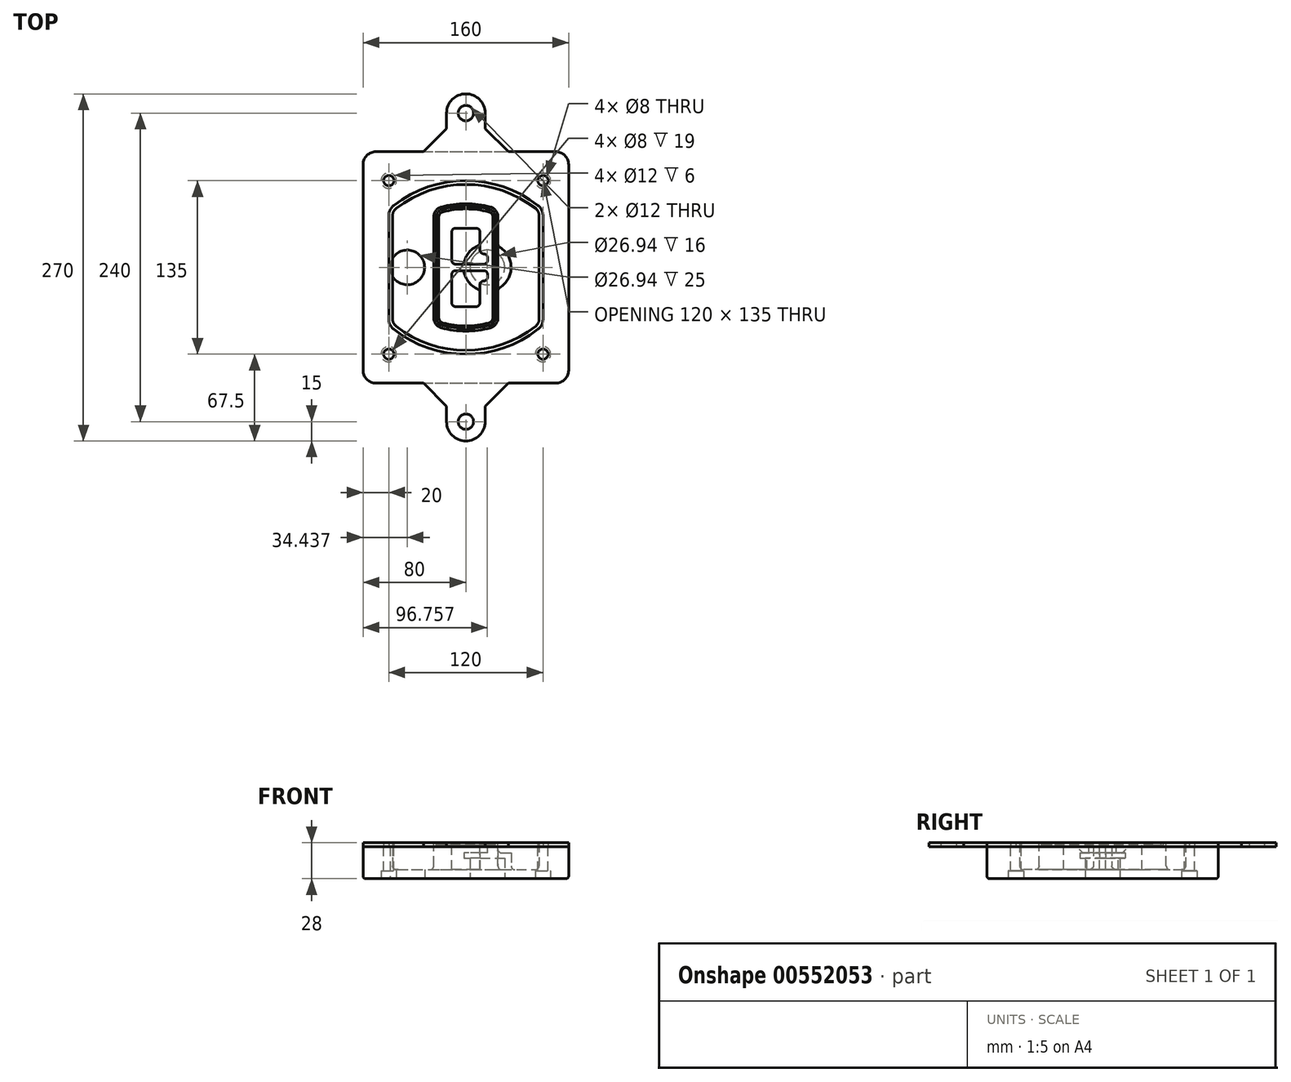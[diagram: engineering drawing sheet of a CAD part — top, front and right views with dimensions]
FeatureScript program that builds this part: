
annotation { "Feature Type Name" : "Feature", "Feature Type Description" : "" }
export const myFeature = defineFeature(function(context is Context, id is Id, definition is map)
    precondition{}
    {
        {
            var Q0;
            Q0=qCreatedBy(makeId("Top.planeOp"),FACE);
            var sketch = newSketch(context, id + "F0", { "sketchPlane" : qUnion([Q0])});
            skPoint(sketch, "E0.rect.middle", {"position": v(0, 0) * mm});
            skLineSegment(sketch, "E1.bottom", {"start": v(-70, -90) * mm, "end": v(70, -90) * mm});
            skLineSegment(sketch, "E1.top", {"start": v(-70, 90) * mm, "end": v(70, 90) * mm});
            skLineSegment(sketch, "E1.left", {"start": v(-80, -80) * mm, "end": v(-80, 80) * mm});
            skLineSegment(sketch, "E1.right", {"start": v(80, -80) * mm, "end": v(80, 80) * mm});
            skLineSegment(sketch, "E2", {"start": v(-80, 90) * mm, "end": v(80, -90) * mm, "construction": true});
            skLineSegment(sketch, "E3", {"start": v(80, 90) * mm, "end": v(-80, -90) * mm, "construction": true});
            skCircle(sketch, "E4", {"center": v(-60, 67.5) * mm, "radius": 4 * mm});
            skCircle(sketch, "E5", {"center": v(60, 67.5) * mm, "radius": 4 * mm});
            skCircle(sketch, "E6", {"center": v(60, -67.5) * mm, "radius": 4 * mm});
            skCircle(sketch, "E7", {"center": v(-60, -67.5) * mm, "radius": 4 * mm});
            skLineSegment(sketch, "E8", {"start": v(-60, 67.5) * mm, "end": v(60, 67.5) * mm, "construction": true});
            skLineSegment(sketch, "E9", {"start": v(60, 67.5) * mm, "end": v(60, -67.5) * mm, "construction": true});
            skLineSegment(sketch, "E10", {"start": v(60, -67.5) * mm, "end": v(-60, -67.5) * mm, "construction": true});
            skLineSegment(sketch, "E11", {"start": v(-60, -67.5) * mm, "end": v(-60, 67.5) * mm, "construction": true});
            skLineSegment(sketch, "E12", {"start": v(-60, 40.3) * mm, "end": v(-60, -40.3) * mm});
            skLineSegment(sketch, "E13", {"start": v(60, 40.3) * mm, "end": v(60, -40.3) * mm});
            skArc(sketch, "E14", {"start": v(56.15, 48.18) * mm, "mid": v(0, 67.5) * mm, "end": v(-56.15, 48.18) * mm});
            skArc(sketch, "E15", {"start": v(-56.15, -48.18) * mm, "mid": v(0, -67.5) * mm, "end": v(56.15, -48.18) * mm});
            skLineSegment(sketch, "E16", {"start": v(-60, 0) * mm, "end": v(60, 0) * mm, "construction": true});
            skPoint(sketch, "E17.visualSharp", {"position": v(-60, -45) * mm});
            skArc(sketch, "E17.filletArc", {"start": v(-60, -40.3) * mm, "mid": v(-58.99, -44.68) * mm, "end": v(-56.15, -48.18) * mm});
            skPoint(sketch, "E18.visualSharp", {"position": v(-60, 45) * mm});
            skArc(sketch, "E18.filletArc", {"start": v(-56.15, 48.18) * mm, "mid": v(-58.99, 44.68) * mm, "end": v(-60, 40.3) * mm});
            skPoint(sketch, "E19.visualSharp", {"position": v(60, 45) * mm});
            skArc(sketch, "E19.filletArc", {"start": v(60, 40.3) * mm, "mid": v(58.99, 44.68) * mm, "end": v(56.15, 48.18) * mm});
            skPoint(sketch, "E20.visualSharp", {"position": v(60, -45) * mm});
            skArc(sketch, "E20.filletArc", {"start": v(56.15, -48.18) * mm, "mid": v(58.99, -44.68) * mm, "end": v(60, -40.3) * mm});
            skPoint(sketch, "E21.visualSharp", {"position": v(-80, 90) * mm});
            skArc(sketch, "E21.filletArc", {"start": v(-70, 90) * mm, "mid": v(-77.07, 87.07) * mm, "end": v(-80, 80) * mm});
            skPoint(sketch, "E22.visualSharp", {"position": v(80, 90) * mm});
            skArc(sketch, "E22.filletArc", {"start": v(80, 80) * mm, "mid": v(77.07, 87.07) * mm, "end": v(70, 90) * mm});
            skPoint(sketch, "E23.visualSharp", {"position": v(80, -90) * mm});
            skArc(sketch, "E23.filletArc", {"start": v(70, -90) * mm, "mid": v(77.07, -87.07) * mm, "end": v(80, -80) * mm});
            skPoint(sketch, "E24.visualSharp", {"position": v(-80, -90) * mm});
            skArc(sketch, "E24.filletArc", {"start": v(-80, -80) * mm, "mid": v(-77.07, -87.07) * mm, "end": v(-70, -90) * mm});
            skArc(sketch, "E25.0", {"start": v(57, 40.3) * mm, "mid": v(56.3, 43.36) * mm, "end": v(54.3, 45.81) * mm});
            skLineSegment(sketch, "E25.1", {"start": v(57, 40.3) * mm, "end": v(57, -40.3) * mm});
            skArc(sketch, "E25.2", {"start": v(54.3, -45.81) * mm, "mid": v(56.3, -43.36) * mm, "end": v(57, -40.3) * mm});
            skArc(sketch, "E25.3", {"start": v(-54.3, -45.81) * mm, "mid": v(0, -64.5) * mm, "end": v(54.3, -45.81) * mm});
            skArc(sketch, "E25.4", {"start": v(-57, -40.3) * mm, "mid": v(-56.3, -43.36) * mm, "end": v(-54.3, -45.81) * mm});
            skArc(sketch, "E25.5", {"start": v(54.3, 45.81) * mm, "mid": v(0, 64.5) * mm, "end": v(-54.3, 45.81) * mm});
            skLineSegment(sketch, "E25.6", {"start": v(-57, 40.3) * mm, "end": v(-57, -40.3) * mm});
            skArc(sketch, "E25.7", {"start": v(-54.3, 45.81) * mm, "mid": v(-56.3, 43.36) * mm, "end": v(-57, 40.3) * mm});
            skArc(sketch, "E26.0", {"start": v(-58.62, 51.33) * mm, "mid": v(-62.58, 46.43) * mm, "end": v(-64, 40.3) * mm});
            skArc(sketch, "E26.1", {"start": v(58.62, 51.33) * mm, "mid": v(0, 71.5) * mm, "end": v(-58.62, 51.33) * mm});
            skArc(sketch, "E26.2", {"start": v(64, 40.3) * mm, "mid": v(62.58, 46.43) * mm, "end": v(58.62, 51.33) * mm});
            skLineSegment(sketch, "E26.3", {"start": v(64, 40.3) * mm, "end": v(64, -40.3) * mm});
            skArc(sketch, "E26.4", {"start": v(58.62, -51.33) * mm, "mid": v(62.58, -46.43) * mm, "end": v(64, -40.3) * mm});
            skLineSegment(sketch, "E26.5", {"start": v(-64, 40.3) * mm, "end": v(-64, -40.3) * mm});
            skArc(sketch, "E26.6", {"start": v(-58.62, -51.33) * mm, "mid": v(0, -71.5) * mm, "end": v(58.62, -51.33) * mm});
            skArc(sketch, "E26.7", {"start": v(-64, -40.3) * mm, "mid": v(-62.58, -46.43) * mm, "end": v(-58.62, -51.33) * mm});
            skSolve(sketch);
        }
        {
            var Q0;
            Q0=makeQuery(id+"F0.imprint","IMPRINT",FACE,{"disambiguationData":[TD([[makeQuery(id+"F0.imprint","IMPRINT",EDGE,{"derivedFrom":sQuery(id+"F0.wireOp",EDGE,"E1.bottom")}),1.0]])]});
            var Q1;
            Q1=makeQuery(id+"F0.imprint","IMPRINT",FACE,{"disambiguationData":[TD([[makeQuery(id+"F0.imprint","IMPRINT",EDGE,{"derivedFrom":sQuery(id+"F0.wireOp",EDGE,"E12")}),1.0]])]});
            var Q2;
            Q2=makeQuery(id+"F0.imprint","IMPRINT",FACE,{"disambiguationData":[TD([[makeQuery(id+"F0.imprint","IMPRINT",EDGE,{"derivedFrom":sQuery(id+"F0.wireOp",EDGE,"E25.0")}),1.0]])]});
            var Q3;
            Q3=makeQuery(id+"F0.imprint","IMPRINT",FACE,{"disambiguationData":[TD([[makeQuery(id+"F0.imprint","IMPRINT",EDGE,{"derivedFrom":sQuery(id+"F0.wireOp",EDGE,"E12")}),-1.0]])]});
            extrude(context, id + "F1", {"entities" : qUnion([Q0, Q1, Q2, Q3]), "oppositeDirection" : true, "depth" : 25 * mm});
        }
        {
            var Q0;
            Q0=makeQuery(id+"F0.imprint","IMPRINT",FACE,{"disambiguationData":[TD([[makeQuery(id+"F0.imprint","IMPRINT",EDGE,{"derivedFrom":sQuery(id+"F0.wireOp",EDGE,"E12")}),1.0]])]});
            extrude(context, id + "F2", {"entities" : qUnion([Q0]), "operationType" : NewBodyOperationType.ADD, "depth" : 3 * mm});
        }
        {
            var Q0;
            Q0=makeQuery(id+"F0.imprint","IMPRINT",FACE,{"disambiguationData":[TD([[makeQuery(id+"F0.imprint","IMPRINT",EDGE,{"derivedFrom":sQuery(id+"F0.wireOp",EDGE,"E25.0")}),1.0]])]});
            extrude(context, id + "F3", {"entities" : qUnion([Q0]), "operationType" : NewBodyOperationType.REMOVE, "oppositeDirection" : true, "depth" : 18 * mm});
        }
        {
            var Q0;
            Q0=makeQuery(id+"F2.opExtrude","CAP_FACE",FACE,{"disambiguationData":[OSD([sQuery(id+"F0.wireOp",EDGE,"E12"),sQuery(id+"F0.wireOp",EDGE,"E13"),sQuery(id+"F0.wireOp",EDGE,"E14"),sQuery(id+"F0.wireOp",EDGE,"E15"),sQuery(id+"F0.wireOp",EDGE,"E17.filletArc"),sQuery(id+"F0.wireOp",EDGE,"E18.filletArc"),sQuery(id+"F0.wireOp",EDGE,"E19.filletArc"),sQuery(id+"F0.wireOp",EDGE,"E20.filletArc"),sQuery(id+"F0.wireOp",EDGE,"E25.0"),sQuery(id+"F0.wireOp",EDGE,"E25.1"),sQuery(id+"F0.wireOp",EDGE,"E25.2"),sQuery(id+"F0.wireOp",EDGE,"E25.3"),sQuery(id+"F0.wireOp",EDGE,"E25.4"),sQuery(id+"F0.wireOp",EDGE,"E25.5"),sQuery(id+"F0.wireOp",EDGE,"E25.6"),sQuery(id+"F0.wireOp",EDGE,"E25.7")])],"isStart":false});
            var sketch = newSketch(context, id + "F4", { "sketchPlane" : qUnion([Q0])});
            skArc(sketch, "E27.0", {"start": v(-19.08, -46.97) * mm, "mid": v(0, -49.5) * mm, "end": v(19.08, -46.97) * mm});
            skArc(sketch, "E28.0", {"start": v(19.08, 46.97) * mm, "mid": v(0, 49.5) * mm, "end": v(-19.08, 46.97) * mm});
            skLineSegment(sketch, "E29", {"start": v(-25, 39.25) * mm, "end": v(-25, -39.25) * mm});
            skLineSegment(sketch, "E30", {"start": v(25, 39.25) * mm, "end": v(25, -39.25) * mm});
            skLineSegment(sketch, "E31", {"start": v(-25, 45.1) * mm, "end": v(25, 45.1) * mm, "construction": true});
            skLineSegment(sketch, "E32", {"start": v(-25, -45.1) * mm, "end": v(25, -45.1) * mm, "construction": true});
            skPoint(sketch, "E33.visualSharp", {"position": v(-25, 45.1) * mm});
            skArc(sketch, "E33.filletArc", {"start": v(-19.08, 46.97) * mm, "mid": v(-23.35, 44.11) * mm, "end": v(-25, 39.25) * mm});
            skPoint(sketch, "E34.visualSharp", {"position": v(25, 45.1) * mm});
            skArc(sketch, "E34.filletArc", {"start": v(25, 39.25) * mm, "mid": v(23.35, 44.11) * mm, "end": v(19.08, 46.97) * mm});
            skPoint(sketch, "E35.visualSharp", {"position": v(25, -45.1) * mm});
            skArc(sketch, "E35.filletArc", {"start": v(19.08, -46.97) * mm, "mid": v(23.35, -44.11) * mm, "end": v(25, -39.25) * mm});
            skPoint(sketch, "E36.visualSharp", {"position": v(-25, -45.1) * mm});
            skArc(sketch, "E36.filletArc", {"start": v(-25, -39.25) * mm, "mid": v(-23.35, -44.11) * mm, "end": v(-19.08, -46.97) * mm});
            skArc(sketch, "E37.0", {"start": v(54.3, 45.81) * mm, "mid": v(0, 64.5) * mm, "end": v(-54.3, 45.81) * mm});
            skArc(sketch, "E37.1", {"start": v(-54.3, 45.81) * mm, "mid": v(-56.3, 43.36) * mm, "end": v(-57, 40.3) * mm});
            skLineSegment(sketch, "E37.2", {"start": v(-57, 40.3) * mm, "end": v(-57, -40.3) * mm});
            skArc(sketch, "E37.3", {"start": v(-57, -40.3) * mm, "mid": v(-56.3, -43.36) * mm, "end": v(-54.3, -45.81) * mm});
            skArc(sketch, "E37.4", {"start": v(-54.3, -45.81) * mm, "mid": v(0, -64.5) * mm, "end": v(54.3, -45.81) * mm});
            skArc(sketch, "E37.5", {"start": v(54.3, -45.81) * mm, "mid": v(56.3, -43.36) * mm, "end": v(57, -40.3) * mm});
            skLineSegment(sketch, "E37.6", {"start": v(57, 40.3) * mm, "end": v(57, -40.3) * mm});
            skArc(sketch, "E37.7", {"start": v(57, 40.3) * mm, "mid": v(56.3, 43.36) * mm, "end": v(54.3, 45.81) * mm});
            skLineSegment(sketch, "E38.0", {"start": v(23, 39.25) * mm, "end": v(23, -39.25) * mm});
            skArc(sketch, "E38.1", {"start": v(18.56, -45.04) * mm, "mid": v(21.76, -42.9) * mm, "end": v(23, -39.25) * mm});
            skArc(sketch, "E38.2", {"start": v(-18.56, -45.04) * mm, "mid": v(0, -47.5) * mm, "end": v(18.56, -45.04) * mm});
            skArc(sketch, "E38.3", {"start": v(-23, -39.25) * mm, "mid": v(-21.76, -42.9) * mm, "end": v(-18.56, -45.04) * mm});
            skLineSegment(sketch, "E38.4", {"start": v(-23, 39.25) * mm, "end": v(-23, -39.25) * mm});
            skArc(sketch, "E38.5", {"start": v(23, 39.25) * mm, "mid": v(21.76, 42.9) * mm, "end": v(18.56, 45.04) * mm});
            skArc(sketch, "E38.6", {"start": v(-18.56, 45.04) * mm, "mid": v(-21.76, 42.9) * mm, "end": v(-23, 39.25) * mm});
            skArc(sketch, "E38.7", {"start": v(18.56, 45.04) * mm, "mid": v(0, 47.5) * mm, "end": v(-18.56, 45.04) * mm});
            skArc(sketch, "E39.0", {"start": v(21, 39.25) * mm, "mid": v(20.18, 41.68) * mm, "end": v(18.04, 43.1) * mm});
            skLineSegment(sketch, "E39.1", {"start": v(21, 39.25) * mm, "end": v(21, -39.25) * mm});
            skArc(sketch, "E39.2", {"start": v(18.04, -43.1) * mm, "mid": v(20.18, -41.68) * mm, "end": v(21, -39.25) * mm});
            skArc(sketch, "E39.3", {"start": v(-18.04, -43.1) * mm, "mid": v(0, -45.5) * mm, "end": v(18.04, -43.1) * mm});
            skArc(sketch, "E39.4", {"start": v(-21, -39.25) * mm, "mid": v(-20.18, -41.68) * mm, "end": v(-18.04, -43.1) * mm});
            skArc(sketch, "E39.5", {"start": v(18.04, 43.1) * mm, "mid": v(0, 45.5) * mm, "end": v(-18.04, 43.1) * mm});
            skLineSegment(sketch, "E39.6", {"start": v(-21, 39.25) * mm, "end": v(-21, -39.25) * mm});
            skArc(sketch, "E39.7", {"start": v(-18.04, 43.1) * mm, "mid": v(-20.18, 41.68) * mm, "end": v(-21, 39.25) * mm});
            skLineSegment(sketch, "E40", {"start": v(-25, 0) * mm, "end": v(25, 0) * mm, "construction": true});
            skLineSegment(sketch, "E41", {"start": v(-11, 5.5) * mm, "end": v(-11, 27.5) * mm});
            skLineSegment(sketch, "E42", {"start": v(-8, 30.5) * mm, "end": v(8, 30.5) * mm});
            skLineSegment(sketch, "E43", {"start": v(11, 27.5) * mm, "end": v(11, 13.5) * mm});
            skLineSegment(sketch, "E44", {"start": v(14, 10.5) * mm, "end": v(14, 10.5) * mm});
            skLineSegment(sketch, "E45", {"start": v(17, 7.5) * mm, "end": v(17, 5.5) * mm});
            skLineSegment(sketch, "E46", {"start": v(14, 2.5) * mm, "end": v(-8, 2.5) * mm});
            skPoint(sketch, "E47.visualSharp", {"position": v(-11, 30.5) * mm});
            skArc(sketch, "E47.filletArc", {"start": v(-8, 30.5) * mm, "mid": v(-10.12, 29.62) * mm, "end": v(-11, 27.5) * mm});
            skPoint(sketch, "E48.visualSharp", {"position": v(11, 30.5) * mm});
            skArc(sketch, "E48.filletArc", {"start": v(11, 27.5) * mm, "mid": v(10.12, 29.62) * mm, "end": v(8, 30.5) * mm});
            skPoint(sketch, "E49.visualSharp", {"position": v(11, 10.5) * mm});
            skArc(sketch, "E49.filletArc", {"start": v(11, 13.5) * mm, "mid": v(11.88, 11.38) * mm, "end": v(14, 10.5) * mm});
            skPoint(sketch, "E50.visualSharp", {"position": v(17, 10.5) * mm});
            skArc(sketch, "E50.filletArc", {"start": v(17, 7.5) * mm, "mid": v(16.12, 9.62) * mm, "end": v(14, 10.5) * mm});
            skPoint(sketch, "E51.visualSharp", {"position": v(17, 2.5) * mm});
            skArc(sketch, "E51.filletArc", {"start": v(14, 2.5) * mm, "mid": v(16.12, 3.38) * mm, "end": v(17, 5.5) * mm});
            skPoint(sketch, "E52.visualSharp", {"position": v(-11, 2.5) * mm});
            skArc(sketch, "E52.filletArc", {"start": v(-11, 5.5) * mm, "mid": v(-10.12, 3.38) * mm, "end": v(-8, 2.5) * mm});
            skLineSegment(sketch, "E53.0.MirrorCS", {"start": v(14, -2.5) * mm, "end": v(-8, -2.5) * mm});
            skArc(sketch, "E54.0.MirrorCS", {"start": v(-11, -5.5) * mm, "mid": v(-10.12, -3.38) * mm, "end": v(-8, -2.5) * mm});
            skLineSegment(sketch, "E55.0.MirrorCS", {"start": v(-11, -5.5) * mm, "end": v(-11, -27.5) * mm});
            skArc(sketch, "E56.0.MirrorCS", {"start": v(-8, -30.5) * mm, "mid": v(-10.12, -29.62) * mm, "end": v(-11, -27.5) * mm});
            skLineSegment(sketch, "E57.0.MirrorCS", {"start": v(-8, -30.5) * mm, "end": v(8, -30.5) * mm});
            skArc(sketch, "E58.0.MirrorCS", {"start": v(11, -27.5) * mm, "mid": v(10.12, -29.62) * mm, "end": v(8, -30.5) * mm});
            skLineSegment(sketch, "E59.0.MirrorCS", {"start": v(11, -27.5) * mm, "end": v(11, -13.5) * mm});
            skArc(sketch, "E60.0.MirrorCS", {"start": v(11, -13.5) * mm, "mid": v(11.88, -11.38) * mm, "end": v(14, -10.5) * mm});
            skArc(sketch, "E61.0.MirrorCS", {"start": v(17, -7.5) * mm, "mid": v(16.12, -9.62) * mm, "end": v(14, -10.5) * mm});
            skLineSegment(sketch, "E62.0.MirrorCS", {"start": v(17, -7.5) * mm, "end": v(17, -5.5) * mm});
            skArc(sketch, "E63.0.MirrorCS", {"start": v(14, -2.5) * mm, "mid": v(16.12, -3.38) * mm, "end": v(17, -5.5) * mm});
            skSolve(sketch);
        }
        {
            var Q0;
            Q0=makeQuery(id+"F4.imprint","IMPRINT",FACE,{"disambiguationData":[TD([[makeQuery(id+"F4.imprint","IMPRINT",EDGE,{"derivedFrom":sQuery(id+"F4.wireOp",EDGE,"E27.0")}),1.0]])]});
            var Q1;
            Q1=makeQuery(id+"F4.imprint","IMPRINT",FACE,{"disambiguationData":[TD([[makeQuery(id+"F4.imprint","IMPRINT",EDGE,{"derivedFrom":sQuery(id+"F4.wireOp",EDGE,"E38.0")}),-1.0]])]});
            var Q2;
            Q2=makeQuery(id+"F4.imprint","IMPRINT",FACE,{"disambiguationData":[TD([[makeQuery(id+"F4.imprint","IMPRINT",EDGE,{"derivedFrom":sQuery(id+"F4.wireOp",EDGE,"E39.0")}),1.0]])]});
            extrude(context, id + "F5", {"entities" : qUnion([Q0, Q1, Q2]), "operationType" : NewBodyOperationType.ADD, "endBound" : BoundingType.UP_TO_NEXT, "oppositeDirection" : true, "depth" : 25 * mm});
        }
        {
            var Q0;
            Q0=makeQuery(id+"F4.imprint","IMPRINT",FACE,{"disambiguationData":[TD([[makeQuery(id+"F4.imprint","IMPRINT",EDGE,{"derivedFrom":sQuery(id+"F4.wireOp",EDGE,"E38.0")}),-1.0]])]});
            extrude(context, id + "F6", {"entities" : qUnion([Q0]), "operationType" : NewBodyOperationType.REMOVE, "oppositeDirection" : true, "depth" : 2 * mm});
        }
        {
            var Q0;
            Q0=makeQuery(id+"F1.opExtrude","CAP_FACE",FACE,{"disambiguationData":[OSD([sQuery(id+"F0.wireOp",EDGE,"E1.bottom"),sQuery(id+"F0.wireOp",EDGE,"E1.top"),sQuery(id+"F0.wireOp",EDGE,"E1.left"),sQuery(id+"F0.wireOp",EDGE,"E1.right"),sQuery(id+"F0.wireOp",EDGE,"E4"),sQuery(id+"F0.wireOp",EDGE,"E5"),sQuery(id+"F0.wireOp",EDGE,"E6"),sQuery(id+"F0.wireOp",EDGE,"E7"),sQuery(id+"F0.wireOp",EDGE,"E21.filletArc"),sQuery(id+"F0.wireOp",EDGE,"E22.filletArc"),sQuery(id+"F0.wireOp",EDGE,"E23.filletArc"),sQuery(id+"F0.wireOp",EDGE,"E24.filletArc")])],"isStart":false});
            var sketch = newSketch(context, id + "F7", { "sketchPlane" : qUnion([Q0])});
            skCircle(sketch, "E64", {"center": v(16.76, 0) * mm, "radius": 13.47 * mm});
            skCircle(sketch, "E65", {"center": v(-45.56, 0) * mm, "radius": 13.47 * mm});
            skLineSegment(sketch, "E66", {"start": v(80, 0) * mm, "end": v(-80, 0) * mm});
            skCircle(sketch, "E67", {"center": v(16.76, 0) * mm, "radius": 18.47 * mm});
            skCircle(sketch, "E68", {"center": v(60, -67.5) * mm, "radius": 6 * mm});
            skCircle(sketch, "E69", {"center": v(-60, -67.5) * mm, "radius": 6 * mm});
            skCircle(sketch, "E70", {"center": v(-60, 67.5) * mm, "radius": 6 * mm});
            skCircle(sketch, "E71", {"center": v(60, 67.5) * mm, "radius": 6 * mm});
            skSolve(sketch);
        }
        {
            var Q0;
            {var subQ1=sQuery(id+"F7.wireOp",EDGE,"E66");var subQ4=sQuery(id+"F7.wireOp",EDGE,"E64");var subQ6=makeQuery(id+"F7.imprint","INTERSECT",VERTEX,{"disambiguationData":[OD(0.0)],"derivedFrom":[subQ4,subQ1]});Q0=makeQuery(id+"F7.imprint","IMPRINT",FACE,{"disambiguationData":[TD([[makeQuery(id+"F7.imprint","IMPRINT",EDGE,{"disambiguationData":[TD([[subQ6,-1.0]])],"derivedFrom":subQ4}),-1.0]])]});}
            var Q1;
            {var subQ0=sQuery(id+"F7.wireOp",EDGE,"E66");var subQ1=sQuery(id+"F7.wireOp",EDGE,"E64");var subQ3=makeQuery(id+"F7.imprint","INTERSECT",VERTEX,{"disambiguationData":[OD(0.0)],"derivedFrom":[subQ1,subQ0]});Q1=makeQuery(id+"F7.imprint","IMPRINT",FACE,{"disambiguationData":[TD([[makeQuery(id+"F7.imprint","IMPRINT",EDGE,{"disambiguationData":[TD([[subQ3,-1.0]])],"derivedFrom":subQ1}),1.0]])]});}
            var Q2;
            {var subQ0=sQuery(id+"F7.wireOp",EDGE,"E66");var subQ1=sQuery(id+"F7.wireOp",EDGE,"E64");var subQ3=makeQuery(id+"F7.imprint","INTERSECT",VERTEX,{"disambiguationData":[OD(0.0)],"derivedFrom":[subQ1,subQ0]});Q2=makeQuery(id+"F7.imprint","IMPRINT",FACE,{"disambiguationData":[TD([[makeQuery(id+"F7.imprint","IMPRINT",EDGE,{"disambiguationData":[TD([[subQ3,1.0]])],"derivedFrom":subQ1}),1.0]])]});}
            var Q3;
            {var subQ1=sQuery(id+"F7.wireOp",EDGE,"E66");var subQ4=sQuery(id+"F7.wireOp",EDGE,"E64");var subQ6=makeQuery(id+"F7.imprint","INTERSECT",VERTEX,{"disambiguationData":[OD(0.0)],"derivedFrom":[subQ4,subQ1]});Q3=makeQuery(id+"F7.imprint","IMPRINT",FACE,{"disambiguationData":[TD([[makeQuery(id+"F7.imprint","IMPRINT",EDGE,{"disambiguationData":[TD([[subQ6,1.0]])],"derivedFrom":subQ4}),-1.0]])]});}
            extrude(context, id + "F8", {"entities" : qUnion([Q0, Q1, Q2, Q3]), "operationType" : NewBodyOperationType.ADD, "oppositeDirection" : true, "depth" : 20 * mm});
        }
        {
            var Q0;
            {var subQ0=sQuery(id+"F7.wireOp",EDGE,"E66");var subQ1=sQuery(id+"F7.wireOp",EDGE,"E64");var subQ3=makeQuery(id+"F7.imprint","INTERSECT",VERTEX,{"disambiguationData":[OD(0.0)],"derivedFrom":[subQ1,subQ0]});Q0=makeQuery(id+"F7.imprint","IMPRINT",FACE,{"disambiguationData":[TD([[makeQuery(id+"F7.imprint","IMPRINT",EDGE,{"disambiguationData":[TD([[subQ3,-1.0]])],"derivedFrom":subQ1}),1.0]])]});}
            var Q1;
            {var subQ0=sQuery(id+"F7.wireOp",EDGE,"E66");var subQ1=sQuery(id+"F7.wireOp",EDGE,"E64");var subQ3=makeQuery(id+"F7.imprint","INTERSECT",VERTEX,{"disambiguationData":[OD(0.0)],"derivedFrom":[subQ1,subQ0]});Q1=makeQuery(id+"F7.imprint","IMPRINT",FACE,{"disambiguationData":[TD([[makeQuery(id+"F7.imprint","IMPRINT",EDGE,{"disambiguationData":[TD([[subQ3,1.0]])],"derivedFrom":subQ1}),1.0]])]});}
            extrude(context, id + "F9", {"entities" : qUnion([Q0, Q1]), "operationType" : NewBodyOperationType.REMOVE, "oppositeDirection" : true, "depth" : 16 * mm});
        }
        {
            var Q0;
            {var subQ0=sQuery(id+"F7.wireOp",EDGE,"E66");var subQ1=sQuery(id+"F7.wireOp",EDGE,"E65");var subQ3=makeQuery(id+"F7.imprint","INTERSECT",VERTEX,{"disambiguationData":[OD(0.0)],"derivedFrom":[subQ1,subQ0]});Q0=makeQuery(id+"F7.imprint","IMPRINT",FACE,{"disambiguationData":[TD([[makeQuery(id+"F7.imprint","IMPRINT",EDGE,{"disambiguationData":[TD([[subQ3,-1.0]])],"derivedFrom":subQ1}),1.0]])]});}
            var Q1;
            {var subQ0=sQuery(id+"F7.wireOp",EDGE,"E66");var subQ1=sQuery(id+"F7.wireOp",EDGE,"E65");var subQ3=makeQuery(id+"F7.imprint","INTERSECT",VERTEX,{"disambiguationData":[OD(0.0)],"derivedFrom":[subQ1,subQ0]});Q1=makeQuery(id+"F7.imprint","IMPRINT",FACE,{"disambiguationData":[TD([[makeQuery(id+"F7.imprint","IMPRINT",EDGE,{"disambiguationData":[TD([[subQ3,1.0]])],"derivedFrom":subQ1}),1.0]])]});}
            extrude(context, id + "F10", {"entities" : qUnion([Q0, Q1]), "operationType" : NewBodyOperationType.REMOVE, "oppositeDirection" : true, "depth" : 25 * mm});
        }
        {
            var Q0;
            Q0=makeQuery(id+"F7.imprint","IMPRINT",FACE,{"disambiguationData":[TD([[makeQuery(id+"F7.imprint","IMPRINT",EDGE,{"derivedFrom":sQuery(id+"F7.wireOp",EDGE,"E68")}),1.0]])]});
            var Q1;
            Q1=makeQuery(id+"F7.imprint","IMPRINT",FACE,{"disambiguationData":[TD([[makeQuery(id+"F7.imprint","IMPRINT",EDGE,{"derivedFrom":makeQuery(id+"F1.opExtrude","CAP_EDGE",EDGE,{"disambiguationData":[OSD([sQuery(id+"F0.wireOp",EDGE,"E5")])],"isStart":false})}),-1.0]])]});
            var Q2;
            Q2=makeQuery(id+"F7.imprint","IMPRINT",FACE,{"disambiguationData":[TD([[makeQuery(id+"F7.imprint","IMPRINT",EDGE,{"derivedFrom":sQuery(id+"F7.wireOp",EDGE,"E69")}),1.0]])]});
            var Q3;
            Q3=makeQuery(id+"F7.imprint","IMPRINT",FACE,{"disambiguationData":[TD([[makeQuery(id+"F7.imprint","IMPRINT",EDGE,{"derivedFrom":makeQuery(id+"F1.opExtrude","CAP_EDGE",EDGE,{"disambiguationData":[OSD([sQuery(id+"F0.wireOp",EDGE,"E4")])],"isStart":false})}),-1.0]])]});
            var Q4;
            Q4=makeQuery(id+"F7.imprint","IMPRINT",FACE,{"disambiguationData":[TD([[makeQuery(id+"F7.imprint","IMPRINT",EDGE,{"derivedFrom":sQuery(id+"F7.wireOp",EDGE,"E70")}),1.0]])]});
            var Q5;
            Q5=makeQuery(id+"F7.imprint","IMPRINT",FACE,{"disambiguationData":[TD([[makeQuery(id+"F7.imprint","IMPRINT",EDGE,{"derivedFrom":makeQuery(id+"F1.opExtrude","CAP_EDGE",EDGE,{"disambiguationData":[OSD([sQuery(id+"F0.wireOp",EDGE,"E7")])],"isStart":false})}),-1.0]])]});
            var Q6;
            Q6=makeQuery(id+"F7.imprint","IMPRINT",FACE,{"disambiguationData":[TD([[makeQuery(id+"F7.imprint","IMPRINT",EDGE,{"derivedFrom":sQuery(id+"F7.wireOp",EDGE,"E71")}),1.0]])]});
            var Q7;
            Q7=makeQuery(id+"F7.imprint","IMPRINT",FACE,{"disambiguationData":[TD([[makeQuery(id+"F7.imprint","IMPRINT",EDGE,{"derivedFrom":makeQuery(id+"F1.opExtrude","CAP_EDGE",EDGE,{"disambiguationData":[OSD([sQuery(id+"F0.wireOp",EDGE,"E6")])],"isStart":false})}),-1.0]])]});
            extrude(context, id + "F11", {"entities" : qUnion([Q0, Q1, Q2, Q3, Q4, Q5, Q6, Q7]), "operationType" : NewBodyOperationType.REMOVE, "oppositeDirection" : true, "depth" : 6 * mm});
        }
        {
            var Q0;
            Q0=makeQuery(id+"F9.boolean.opBoolean","COPY",FACE,{"derivedFrom":makeQuery(id+"F9.opExtrude","CAP_FACE",FACE,{"disambiguationData":[OSD([sQuery(id+"F7.wireOp",EDGE,"E64")])],"isStart":false})});
            var sketch = newSketch(context, id + "F12", { "sketchPlane" : qUnion([Q0])});
            skArc(sketch, "E72.0", {"start": v(11, 17.55) * mm, "mid": v(2.57, 11.82) * mm, "end": v(-1.54, 2.5) * mm});
            skArc(sketch, "E72.1", {"start": v(-1.54, -2.5) * mm, "mid": v(2.57, -11.82) * mm, "end": v(11, -17.55) * mm});
            skLineSegment(sketch, "E73", {"start": v(-1.54, -2.5) * mm, "end": v(14, -2.5) * mm});
            skLineSegment(sketch, "E74.0", {"start": v(14, 2.5) * mm, "end": v(-1.54, 2.5) * mm});
            skArc(sketch, "E74.1", {"start": v(14, 2.5) * mm, "mid": v(16.12, 3.38) * mm, "end": v(17, 5.5) * mm});
            skLineSegment(sketch, "E74.2", {"start": v(17, 7.5) * mm, "end": v(17, 5.5) * mm});
            skArc(sketch, "E74.3", {"start": v(17, 7.5) * mm, "mid": v(16.12, 9.62) * mm, "end": v(14, 10.5) * mm});
            skArc(sketch, "E74.4", {"start": v(11, 13.5) * mm, "mid": v(11.88, 11.38) * mm, "end": v(14, 10.5) * mm});
            skLineSegment(sketch, "E74.5", {"start": v(11, 17.55) * mm, "end": v(11, 13.5) * mm});
            skLineSegment(sketch, "E74.7", {"start": v(14, -2.5) * mm, "end": v(-1.54, -2.5) * mm});
            skArc(sketch, "E74.8", {"start": v(14, -2.5) * mm, "mid": v(16.12, -3.38) * mm, "end": v(17, -5.5) * mm});
            skLineSegment(sketch, "E74.9", {"start": v(17, -7.5) * mm, "end": v(17, -5.5) * mm});
            skArc(sketch, "E74.10", {"start": v(17, -7.5) * mm, "mid": v(16.12, -9.62) * mm, "end": v(14, -10.5) * mm});
            skArc(sketch, "E74.11", {"start": v(11, -13.5) * mm, "mid": v(11.88, -11.38) * mm, "end": v(14, -10.5) * mm});
            skLineSegment(sketch, "E74.12", {"start": v(11, -17.55) * mm, "end": v(11, -13.5) * mm});
            skPoint(sketch, "E75.orphan", {"position": v(11, -27.5) * mm});
            skPoint(sketch, "E76.orphan", {"position": v(-8, -2.5) * mm});
            skPoint(sketch, "E77.orphan", {"position": v(-8, 2.5) * mm});
            skPoint(sketch, "E78.orphan", {"position": v(11, 27.5) * mm});
            skSolve(sketch);
        }
        {
            var Q0;
            {var subQ7=sQuery(id+"F12.wireOp",EDGE,"E72.0");var subQ14=sQuery(id+"F12.wireOp",EDGE,"E72.1");var subQ16=sQuery(id+"F12.wireOp",EDGE,"E74.1");var subQ18=sQuery(id+"F12.wireOp",EDGE,"E74.8");Q0=qUnion([makeQuery(id+"F12.imprint","IMPRINT",FACE,{"disambiguationData":[TD([[makeQuery(id+"F12.imprint","IMPRINT",EDGE,{"derivedFrom":subQ7}),1.0]])]}),makeQuery(id+"F12.imprint","IMPRINT",FACE,{"disambiguationData":[TD([[makeQuery(id+"F12.imprint","IMPRINT",EDGE,{"derivedFrom":subQ14}),1.0]])]}),makeQuery(id+"F12.imprint","IMPRINT",FACE,{"disambiguationData":[TD([[makeQuery(id+"F12.imprint","IMPRINT",EDGE,{"derivedFrom":subQ16}),1.0]])]}),makeQuery(id+"F12.imprint","IMPRINT",FACE,{"disambiguationData":[TD([[makeQuery(id+"F12.imprint","IMPRINT",EDGE,{"derivedFrom":subQ18}),-1.0]])]})]);}
            var Q1;
            Q1=makeQuery(id+"F5.boolean.opBoolean","SPLIT",FACE,{"disambiguationData":[TD([makeQuery(id+"F5.opExtrude","SWEPT_FACE",FACE,{"disambiguationData":[OSD([sQuery(id+"F4.wireOp",EDGE,"E41")])]})])],"derivedFrom":makeQuery(id+"F3.boolean.opBoolean","COPY",FACE,{"derivedFrom":makeQuery(id+"F3.opExtrude","CAP_FACE",FACE,{"disambiguationData":[OSD([sQuery(id+"F0.wireOp",EDGE,"E25.0"),sQuery(id+"F0.wireOp",EDGE,"E25.1"),sQuery(id+"F0.wireOp",EDGE,"E25.2"),sQuery(id+"F0.wireOp",EDGE,"E25.3"),sQuery(id+"F0.wireOp",EDGE,"E25.4"),sQuery(id+"F0.wireOp",EDGE,"E25.5"),sQuery(id+"F0.wireOp",EDGE,"E25.6"),sQuery(id+"F0.wireOp",EDGE,"E25.7")])],"isStart":false})})});
            extrude(context, id + "F13", {"entities" : qUnion([Q0]), "operationType" : NewBodyOperationType.REMOVE, "endBound" : BoundingType.UP_TO_SURFACE, "endBoundEntityFace" : qUnion([Q1]), "depth" : 25 * mm});
        }
        {
            var Q0;
            Q0=makeQuery(id+"F3.boolean.opBoolean","COPY",EDGE,{"derivedFrom":makeQuery(id+"F3.opExtrude","CAP_EDGE",EDGE,{"disambiguationData":[OSD([sQuery(id+"F0.wireOp",EDGE,"E25.6")])],"isStart":false})});
            var Q1;
            Q1=makeQuery(id+"F8.boolean.opBoolean","INTERSECT",EDGE,{"derivedFrom":[makeQuery(id+"F5.opExtrude","SWEPT_FACE",FACE,{"disambiguationData":[OSD([sQuery(id+"F4.wireOp",EDGE,"E30")])]}),makeQuery(id+"F8.opExtrude","CAP_FACE",FACE,{"disambiguationData":[OSD([sQuery(id+"F7.wireOp",EDGE,"E67")])],"isStart":false})]});
            var Q2;
            Q2=makeQuery(id+"F8.boolean.opBoolean","INTERSECT",EDGE,{"disambiguationData":[OD(1.0)],"derivedFrom":[makeQuery(id+"F5.opExtrude","SWEPT_FACE",FACE,{"disambiguationData":[OSD([sQuery(id+"F4.wireOp",EDGE,"E30")])]}),makeQuery(id+"F8.opExtrude","SWEPT_FACE",FACE,{"disambiguationData":[OSD([sQuery(id+"F7.wireOp",EDGE,"E67")])]})]});
            var Q3;
            {var subQ0=sQuery(id+"F4.wireOp",EDGE,"E30");Q3=makeQuery(id+"F8.boolean.opBoolean","SPLIT",EDGE,{"disambiguationData":[TD([makeQuery(id+"F5.opExtrude","SWEPT_FACE",FACE,{"disambiguationData":[OSD([sQuery(id+"F4.wireOp",EDGE,"E35.filletArc")])]})])],"derivedFrom":makeQuery(id+"F5.opExtrude","CAP_EDGE",EDGE,{"disambiguationData":[OSD([subQ0])],"isStart":false})});}
            var Q4;
            {var subQ0=sQuery(id+"F0.wireOp",EDGE,"E25.7");var subQ1=sQuery(id+"F0.wireOp",EDGE,"E25.1");var subQ2=sQuery(id+"F0.wireOp",EDGE,"E25.6");var subQ3=sQuery(id+"F0.wireOp",EDGE,"E25.5");var subQ4=sQuery(id+"F0.wireOp",EDGE,"E25.4");var subQ5=sQuery(id+"F0.wireOp",EDGE,"E25.0");var subQ6=sQuery(id+"F0.wireOp",EDGE,"E25.2");var subQ7=sQuery(id+"F0.wireOp",EDGE,"E25.3");Q4=makeQuery(id+"F8.boolean.opBoolean","INTERSECT",EDGE,{"derivedFrom":[makeQuery(id+"F5.boolean.opBoolean","SPLIT",FACE,{"disambiguationData":[TD([makeQuery(id+"F2.opExtrude","SWEPT_FACE",FACE,{"disambiguationData":[OSD([subQ5])]})])],"derivedFrom":makeQuery(id+"F3.boolean.opBoolean","COPY",FACE,{"derivedFrom":makeQuery(id+"F3.opExtrude","CAP_FACE",FACE,{"disambiguationData":[OSD([subQ5,subQ1,subQ6,subQ7,subQ4,subQ3,subQ2,subQ0])],"isStart":false})})}),makeQuery(id+"F8.opExtrude","SWEPT_FACE",FACE,{"disambiguationData":[OSD([sQuery(id+"F7.wireOp",EDGE,"E67")])]})]});}
            var Q5;
            Q5=makeQuery(id+"F8.boolean.opBoolean","INTERSECT",EDGE,{"disambiguationData":[OD(0.0)],"derivedFrom":[makeQuery(id+"F5.opExtrude","SWEPT_FACE",FACE,{"disambiguationData":[OSD([sQuery(id+"F4.wireOp",EDGE,"E30")])]}),makeQuery(id+"F8.opExtrude","SWEPT_FACE",FACE,{"disambiguationData":[OSD([sQuery(id+"F7.wireOp",EDGE,"E67")])]})]});
            fillet(context, id + "F14", {"entities" : qUnion([Q0, Q1, Q2, Q3, Q4, Q5]), "radius" : 3 * mm, "tangentPropagation" : true, "allowEdgeOverflow" : false});
        }
        {
            var Q0;
            Q0=makeQuery(id+"F1.opExtrude","CAP_EDGE",EDGE,{"disambiguationData":[OSD([sQuery(id+"F0.wireOp",EDGE,"E1.bottom")])],"isStart":false});
            fillet(context, id + "F15", {"entities" : qUnion([Q0]), "radius" : 2 * mm, "tangentPropagation" : true, "allowEdgeOverflow" : false});
        }
        {
            var Q0;
            {var subQ0=sQuery(id+"F0.wireOp",EDGE,"E21.filletArc");var subQ1=sQuery(id+"F0.wireOp",EDGE,"E7");var subQ2=sQuery(id+"F0.wireOp",EDGE,"E6");var subQ3=sQuery(id+"F0.wireOp",EDGE,"E5");var subQ4=sQuery(id+"F0.wireOp",EDGE,"E4");var subQ5=sQuery(id+"F0.wireOp",EDGE,"E22.filletArc");var subQ6=sQuery(id+"F0.wireOp",EDGE,"E1.bottom");var subQ7=sQuery(id+"F0.wireOp",EDGE,"E1.right");var subQ8=sQuery(id+"F0.wireOp",EDGE,"E1.top");var subQ9=sQuery(id+"F0.wireOp",EDGE,"E1.left");var subQ10=sQuery(id+"F0.wireOp",EDGE,"E23.filletArc");var subQ11=sQuery(id+"F0.wireOp",EDGE,"E24.filletArc");Q0=makeQuery(id+"F2.boolean.opBoolean","SPLIT",FACE,{"disambiguationData":[TD([makeQuery(id+"F1.opExtrude","SWEPT_FACE",FACE,{"disambiguationData":[OSD([subQ6])]})])],"derivedFrom":makeQuery(id+"F1.opExtrude","CAP_FACE",FACE,{"disambiguationData":[OSD([subQ6,subQ8,subQ9,subQ7,subQ4,subQ3,subQ2,subQ1,subQ0,subQ5,subQ10,subQ11])],"isStart":true})});}
            var sketch = newSketch(context, id + "F16", { "sketchPlane" : qUnion([Q0])});
            skLineSegment(sketch, "E79.0", {"start": v(-80, -80) * mm, "end": v(-80, 80) * mm});
            skArc(sketch, "E80.0", {"start": v(-70, 90) * mm, "mid": v(-77.07, 87.07) * mm, "end": v(-80, 80) * mm});
            skLineSegment(sketch, "E81.0", {"start": v(-70, 90) * mm, "end": v(70, 90) * mm});
            skArc(sketch, "E82.0", {"start": v(80, 80) * mm, "mid": v(77.07, 87.07) * mm, "end": v(70, 90) * mm});
            skLineSegment(sketch, "E83.0", {"start": v(80, -80) * mm, "end": v(80, 80) * mm});
            skArc(sketch, "E84.0", {"start": v(70, -90) * mm, "mid": v(77.07, -87.07) * mm, "end": v(80, -80) * mm});
            skLineSegment(sketch, "E85.0", {"start": v(-70, -90) * mm, "end": v(70, -90) * mm});
            skArc(sketch, "E86.0", {"start": v(-80, -80) * mm, "mid": v(-77.07, -87.07) * mm, "end": v(-70, -90) * mm});
            skCircle(sketch, "E87.0", {"center": v(-60, -67.5) * mm, "radius": 4 * mm});
            skCircle(sketch, "E88.0", {"center": v(-60, 67.5) * mm, "radius": 4 * mm});
            skCircle(sketch, "E89.0", {"center": v(60, 67.5) * mm, "radius": 4 * mm});
            skCircle(sketch, "E90.0", {"center": v(60, -67.5) * mm, "radius": 4 * mm});
            skLineSegment(sketch, "E91", {"start": v(0, 90) * mm, "end": v(0, 120) * mm, "construction": true});
            skArc(sketch, "E92", {"start": v(-15, 120) * mm, "mid": v(0, 135) * mm, "end": v(15, 120) * mm});
            skCircle(sketch, "E93", {"center": v(0, 120) * mm, "radius": 6 * mm});
            skLineSegment(sketch, "E94", {"start": v(-15, 120) * mm, "end": v(-15, 108) * mm});
            skLineSegment(sketch, "E95", {"start": v(15, 120) * mm, "end": v(15, 108) * mm});
            skLineSegment(sketch, "E96", {"start": v(-15, 108) * mm, "end": v(-33, 90) * mm});
            skLineSegment(sketch, "E97", {"start": v(15, 108) * mm, "end": v(33, 90) * mm});
            skLineSegment(sketch, "E98.0", {"start": v(-60, 40.3) * mm, "end": v(-60, -40.3) * mm});
            skArc(sketch, "E99.0", {"start": v(56.15, 48.18) * mm, "mid": v(0, 67.5) * mm, "end": v(-56.15, 48.18) * mm});
            skArc(sketch, "E100.0", {"start": v(-56.15, 48.18) * mm, "mid": v(-58.99, 44.68) * mm, "end": v(-60, 40.3) * mm});
            skArc(sketch, "E101.0", {"start": v(60, 40.3) * mm, "mid": v(58.99, 44.68) * mm, "end": v(56.15, 48.18) * mm});
            skLineSegment(sketch, "E102.0", {"start": v(60, 40.3) * mm, "end": v(60, -40.3) * mm});
            skArc(sketch, "E103.0", {"start": v(56.15, -48.18) * mm, "mid": v(58.99, -44.68) * mm, "end": v(60, -40.3) * mm});
            skArc(sketch, "E104.0", {"start": v(-60, -40.3) * mm, "mid": v(-58.99, -44.68) * mm, "end": v(-56.15, -48.18) * mm});
            skArc(sketch, "E105.0", {"start": v(-56.15, -48.18) * mm, "mid": v(0, -67.5) * mm, "end": v(56.15, -48.18) * mm});
            skLineSegment(sketch, "E106", {"start": v(-80, 0) * mm, "end": v(80, 0) * mm, "construction": true});
            skLineSegment(sketch, "E107.MirrorCS", {"start": v(-15, -108) * mm, "end": v(-33, -90) * mm});
            skLineSegment(sketch, "E108.MirrorCS", {"start": v(0, -90) * mm, "end": v(0, -120) * mm, "construction": true});
            skLineSegment(sketch, "E109.MirrorCS", {"start": v(-15, -120) * mm, "end": v(-15, -108) * mm});
            skArc(sketch, "E110.MirrorCS", {"start": v(-15, -120) * mm, "mid": v(0, -135) * mm, "end": v(15, -120) * mm});
            skLineSegment(sketch, "E111.MirrorCS", {"start": v(15, -120) * mm, "end": v(15, -108) * mm});
            skLineSegment(sketch, "E112.MirrorCS", {"start": v(15, -108) * mm, "end": v(33, -90) * mm});
            skCircle(sketch, "E113.MirrorC", {"center": v(0, -120) * mm, "radius": 6 * mm});
            skSolve(sketch);
        }
        {
            var Q0;
            Q0 = qSketchRegion(id + "F16", true);
            var Q1;
            Q1=makeQuery(id+"F2.opExtrude","CAP_FACE",FACE,{"disambiguationData":[OSD([sQuery(id+"F0.wireOp",EDGE,"E12"),sQuery(id+"F0.wireOp",EDGE,"E13"),sQuery(id+"F0.wireOp",EDGE,"E14"),sQuery(id+"F0.wireOp",EDGE,"E15"),sQuery(id+"F0.wireOp",EDGE,"E17.filletArc"),sQuery(id+"F0.wireOp",EDGE,"E18.filletArc"),sQuery(id+"F0.wireOp",EDGE,"E19.filletArc"),sQuery(id+"F0.wireOp",EDGE,"E20.filletArc"),sQuery(id+"F0.wireOp",EDGE,"E25.0"),sQuery(id+"F0.wireOp",EDGE,"E25.1"),sQuery(id+"F0.wireOp",EDGE,"E25.2"),sQuery(id+"F0.wireOp",EDGE,"E25.3"),sQuery(id+"F0.wireOp",EDGE,"E25.4"),sQuery(id+"F0.wireOp",EDGE,"E25.5"),sQuery(id+"F0.wireOp",EDGE,"E25.6"),sQuery(id+"F0.wireOp",EDGE,"E25.7")])],"isStart":false});
            extrude(context, id + "F17", {"entities" : qUnion([Q0]), "endBound" : BoundingType.UP_TO_SURFACE, "depth" : 25 * mm, "endBoundEntityFace" : qUnion([Q1]), "offsetDistance" : 25 * mm});
        }
    });
